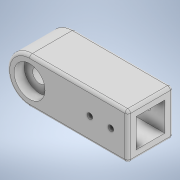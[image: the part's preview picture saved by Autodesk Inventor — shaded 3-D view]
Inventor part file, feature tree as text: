
AUTODESK INVENTOR PART (.ipt)
format: ipt  version: 2020 (Build 240168000, 168)  size: 163,328 bytes
history: native  units: in
note: dims shown in document units (in); Inventor stores cm internally (conversion verified against a paired STEP export)
features: extrude x3, sketch x3, fillet x1
ambient origin geometry x8: Origin, YZ Plane, XZ Plane, XY Plane, X Axis, Y Axis, Z Axis, Center Point
bodies: Solid1 (feature_tree)
feature tree (7):
  extrude  "Extrusion1"  Depth=0.3937in
  extrude  "Extrusion2"  Depth=0.6378in
  extrude  "Extrusion3"  Depth=0.0787in
  fillet  "Fillet1"  Radius=0.5906in
  sketch  "Sketch1"  dims[d1=1.2756in d2=0.3937in]
  sketch  "Sketch2"  dims[d4=0.6378in d5=0.1575in]
  sketch  "Sketch3"  dims[d6=1.6929in d7=0.1575in d8=0.5906in d9=1.2756in d10=1.2756in d11=0.0in d12=0.8071in d13=0.8071in d14=1.9685in d15=0.0in d16=0.8685in d17=0.2835in d18=0.0in d19=0.0787in]
